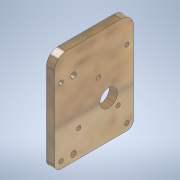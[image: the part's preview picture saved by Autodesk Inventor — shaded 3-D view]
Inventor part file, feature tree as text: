
AUTODESK INVENTOR PART (.ipt)
format: ipt  version: 2020.3 (Build 243373000, 373)  size: 301,568 bytes
history: native  units: mm
features: sketch x7, hole x4, extrude x3, fillet x2, other x1
ambient origin geometry x8: Origin, YZ Plane, XZ Plane, XY Plane, X Axis, Y Axis, Z Axis, Center Point
bodies: Body1 (feature_tree)
feature tree (17):
  other  "ソリッド1"
  extrude  "押し出し1"  Depth=55.5mm
  hole  "穴1"  [1 undecoded]
  hole  "穴2"  [1 undecoded]
  extrude  "押し出し3"  Depth=4.5mm
  extrude  "押し出し4"  Depth=4.5mm
  fillet  "フィレット2"  Radius=4.5mm
  fillet  "フィレット3"  Radius=4.5mm
  hole  "穴3"  [1 undecoded]
  hole  "穴4"  [1 undecoded]
  sketch  "スケッチ1"
  sketch  "スケッチ2"
  sketch  "スケッチ3"
  sketch  "スケッチ4"
  sketch  "スケッチ5"
  sketch  "スケッチ6"
  sketch  "スケッチ7"
note: 4 required parameter values undecoded (feature->parameter linkage not recoverable at this tier; creation-order binding heuristic only, values carry confidence <= 0.55)
